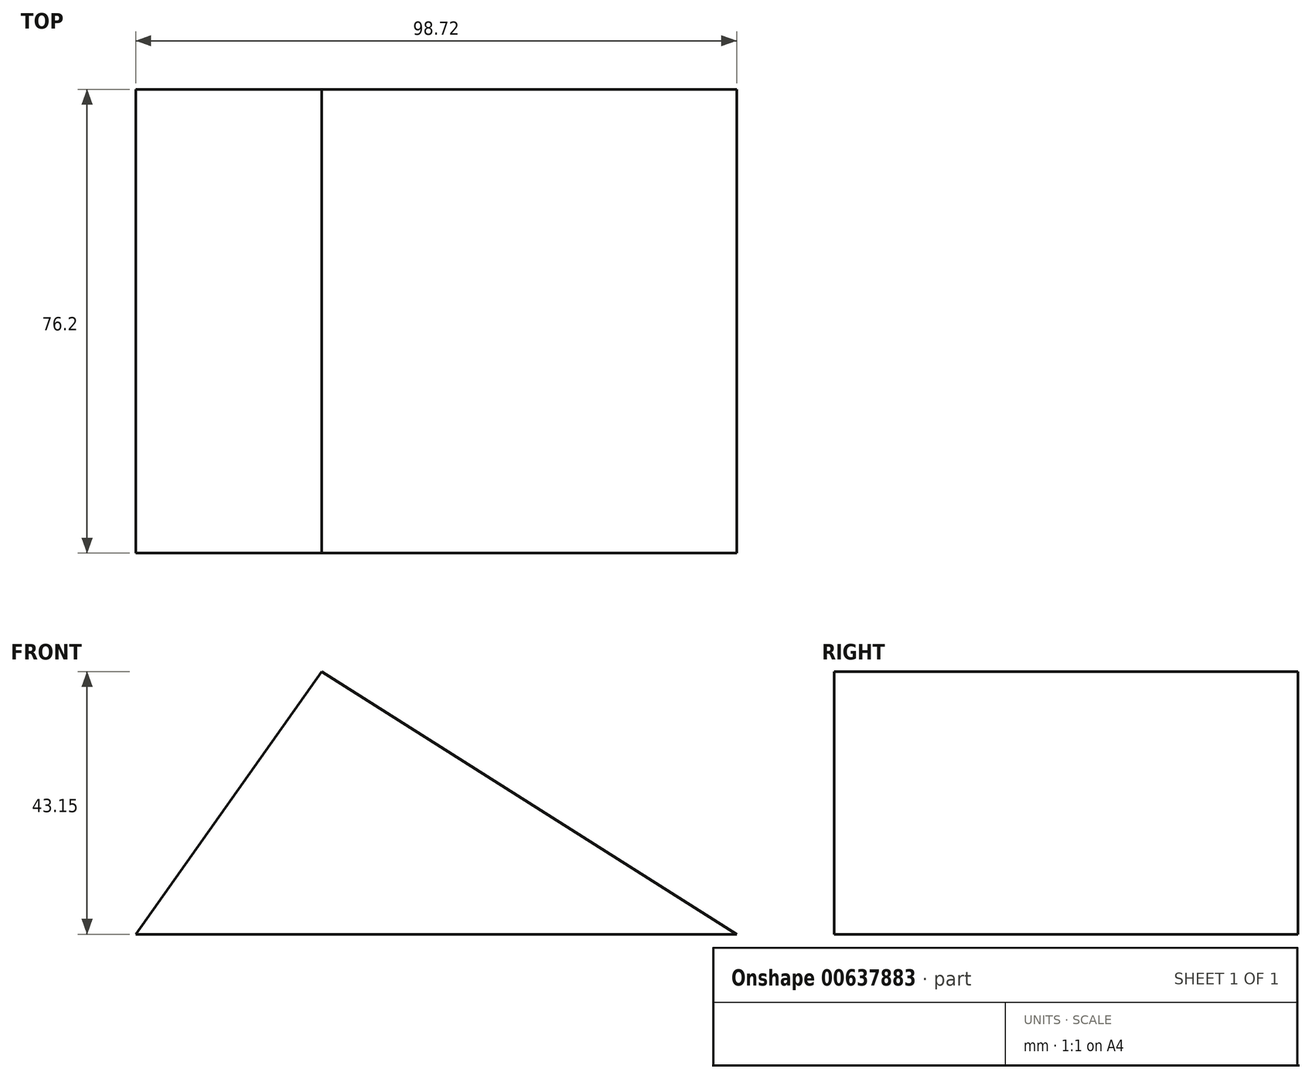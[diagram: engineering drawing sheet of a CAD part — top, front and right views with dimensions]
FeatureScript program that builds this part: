
annotation { "Feature Type Name" : "Feature", "Feature Type Description" : "" }
export const myFeature = defineFeature(function(context is Context, id is Id, definition is map)
    precondition{}
    {
        {
            var Q0;
            Q0=qCreatedBy(makeId("Front.planeOp"),FACE);
            var sketch = newSketch(context, id + "F0", { "sketchPlane" : qUnion([Q0])});
            skLineSegment(sketch, "E0", {"start": v(-12.89, 35.23) * mm, "end": v(55.28, -7.92) * mm});
            skLineSegment(sketch, "E1", {"start": v(55.28, -7.92) * mm, "end": v(-43.44, -7.92) * mm});
            skLineSegment(sketch, "E2", {"start": v(-43.44, -7.92) * mm, "end": v(-12.89, 35.23) * mm});
            skSolve(sketch);
        }
        {
            var Q0;
            Q0 = qSketchRegion(id + "F0", true);
            extrude(context, id + "F1", {"entities" : qUnion([Q0]), "depth" : 76.2 * mm, "offsetDistance" : 25.4 * mm});
        }
    });
